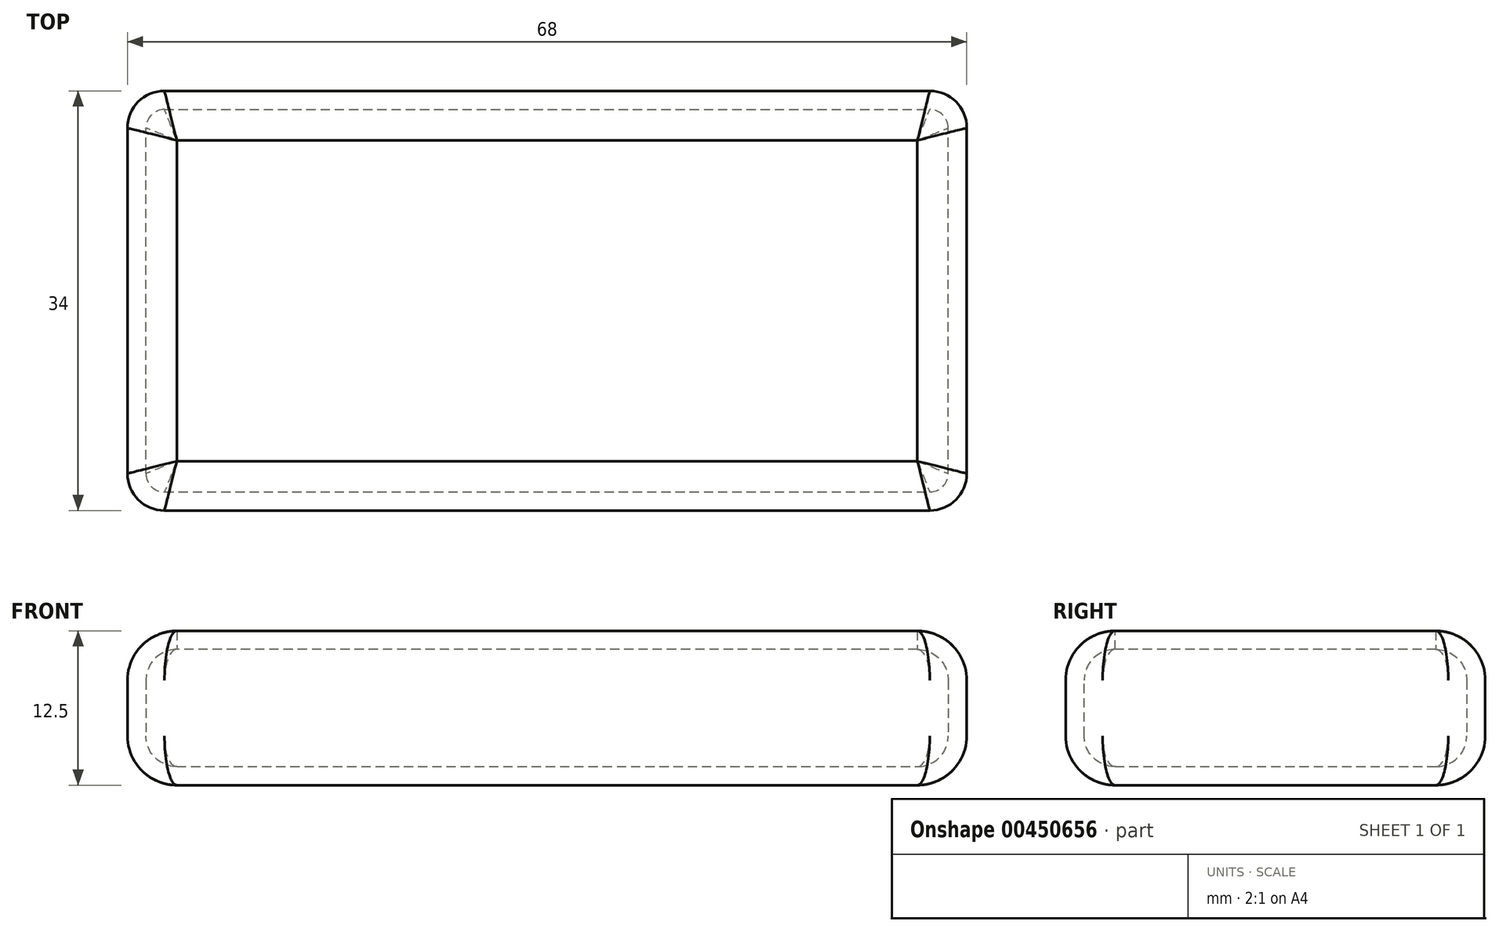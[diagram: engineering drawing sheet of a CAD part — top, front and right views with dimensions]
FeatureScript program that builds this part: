
annotation { "Feature Type Name" : "Feature", "Feature Type Description" : "" }
export const myFeature = defineFeature(function(context is Context, id is Id, definition is map)
    precondition{}
    {
        {
            var Q0;
            Q0=qCreatedBy(makeId("Top.planeOp"),FACE);
            var sketch = newSketch(context, id + "F0", { "sketchPlane" : qUnion([Q0])});
            skLineSegment(sketch, "E0.bottom", {"start": v(-37.8, 6.4) * mm, "end": v(24.2, 6.4) * mm});
            skLineSegment(sketch, "E0.top", {"start": v(-37.8, -27.6) * mm, "end": v(24.2, -27.6) * mm});
            skLineSegment(sketch, "E0.left", {"start": v(-40.8, 3.4) * mm, "end": v(-40.8, -24.6) * mm});
            skLineSegment(sketch, "E0.right", {"start": v(27.2, 3.4) * mm, "end": v(27.2, -24.6) * mm});
            skPoint(sketch, "E1.visualSharp", {"position": v(-40.8, 6.4) * mm});
            skArc(sketch, "E1.filletArc", {"start": v(-37.8, 6.4) * mm, "mid": v(-39.91, 5.52) * mm, "end": v(-40.8, 3.4) * mm});
            skPoint(sketch, "E2.visualSharp", {"position": v(27.2, 6.4) * mm});
            skArc(sketch, "E2.filletArc", {"start": v(27.2, 3.4) * mm, "mid": v(26.33, 5.52) * mm, "end": v(24.2, 6.4) * mm});
            skPoint(sketch, "E3.visualSharp", {"position": v(-40.8, -27.6) * mm});
            skArc(sketch, "E3.filletArc", {"start": v(-40.8, -24.6) * mm, "mid": v(-39.91, -26.73) * mm, "end": v(-37.8, -27.6) * mm});
            skPoint(sketch, "E4.visualSharp", {"position": v(27.2, -27.6) * mm});
            skArc(sketch, "E4.filletArc", {"start": v(24.2, -27.6) * mm, "mid": v(26.33, -26.73) * mm, "end": v(27.2, -24.6) * mm});
            skSolve(sketch);
        }
        {
            var Q0;
            Q0=makeQuery(id+"F0.imprint","IMPRINT",FACE,{"disambiguationData":[TD([[makeQuery(id+"F0.imprint","IMPRINT",EDGE,{"derivedFrom":sQuery(id+"F0.wireOp",EDGE,"E0.bottom")}),-1.0]])]});
            extrude(context, id + "F1", {"entities" : qUnion([Q0]), "depth" : 12.5 * mm});
        }
        {
            var Q0;
            Q0=makeQuery(id+"F1.opExtrude","SWEPT_FACE",FACE,{"disambiguationData":[OSD([sQuery(id+"F0.wireOp",EDGE,"E0.top")])]});
            fillet(context, id + "F2", {"entities" : qUnion([Q0]), "radius" : 4 * mm, "tangentPropagation" : true, "allowEdgeOverflow" : false});
        }
        {
            var Q0;
            Q0=makeQuery(id+"F1.opExtrude","CAP_FACE",FACE,{"disambiguationData":[OSD([sQuery(id+"F0.wireOp",EDGE,"E0.bottom"),sQuery(id+"F0.wireOp",EDGE,"E0.top"),sQuery(id+"F0.wireOp",EDGE,"E0.left"),sQuery(id+"F0.wireOp",EDGE,"E0.right"),sQuery(id+"F0.wireOp",EDGE,"E1.filletArc"),sQuery(id+"F0.wireOp",EDGE,"E2.filletArc"),sQuery(id+"F0.wireOp",EDGE,"E3.filletArc"),sQuery(id+"F0.wireOp",EDGE,"E4.filletArc")])],"isStart":false});
            shell(context, id + "F3", {"entities" : qUnion([Q0]), "thickness" : 1.5 * mm});
        }
    });
